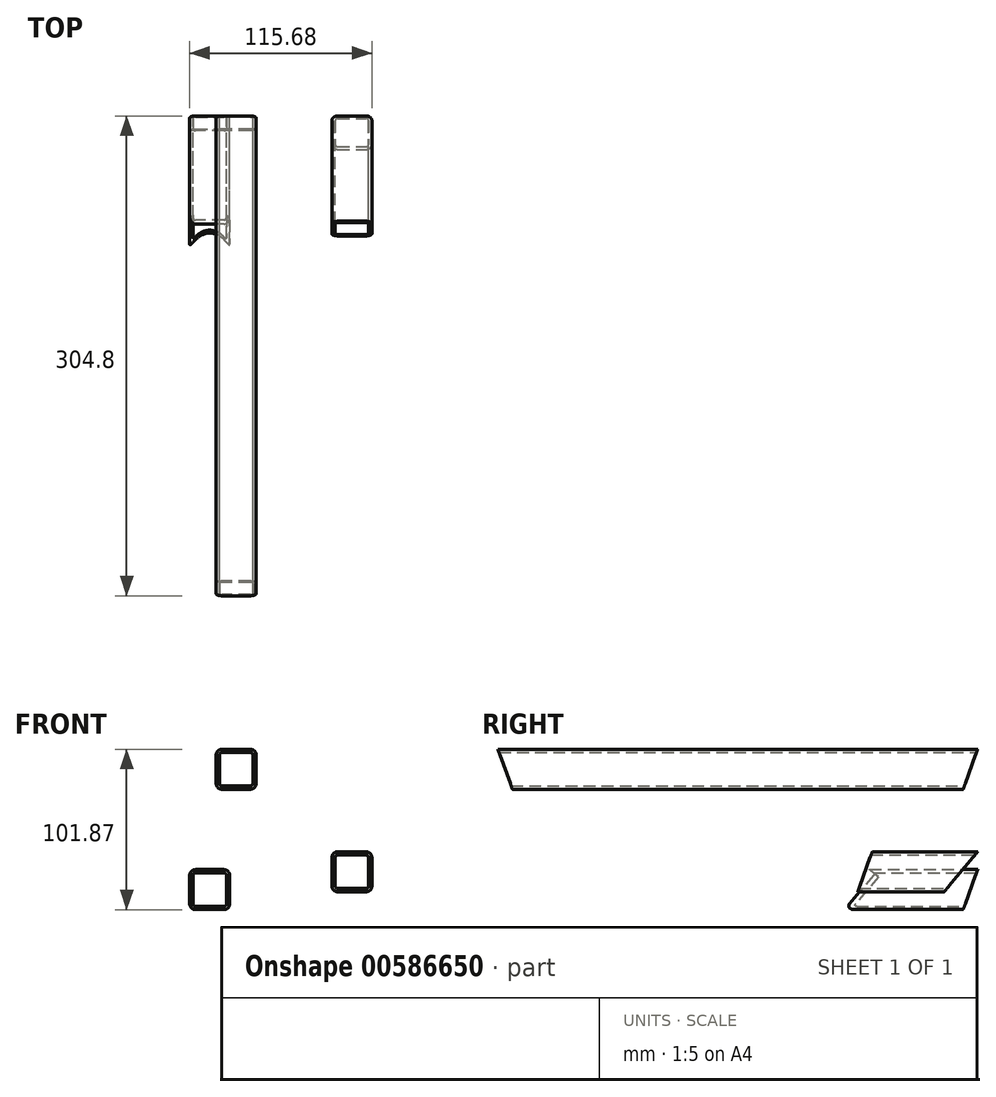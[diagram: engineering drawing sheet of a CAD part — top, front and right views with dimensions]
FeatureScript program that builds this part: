
annotation { "Feature Type Name" : "Feature", "Feature Type Description" : "" }
export const myFeature = defineFeature(function(context is Context, id is Id, definition is map)
    precondition{}
    {
        {
            var Q0;
            Q0=qCreatedBy(makeId("Front.planeOp"),FACE);
            var sketch = newSketch(context, id + "F0", { "sketchPlane" : qUnion([Q0])});
            skLineSegment(sketch, "E0.bottom", {"start": v(-55.98, 51.3) * mm, "end": v(-37.94, 51.3) * mm});
            skLineSegment(sketch, "E0.top", {"start": v(-55.98, 30.06) * mm, "end": v(-37.94, 30.06) * mm});
            skLineSegment(sketch, "E0.left", {"start": v(-57.58, 49.7) * mm, "end": v(-57.58, 31.66) * mm});
            skLineSegment(sketch, "E0.right", {"start": v(-36.34, 49.7) * mm, "end": v(-36.34, 31.66) * mm});
            skPoint(sketch, "E1.visualSharp", {"position": v(-57.58, 51.3) * mm});
            skArc(sketch, "E1.filletArc", {"start": v(-55.98, 51.3) * mm, "mid": v(-57.1, 50.83) * mm, "end": v(-57.58, 49.7) * mm});
            skPoint(sketch, "E2.visualSharp", {"position": v(-36.34, 51.3) * mm});
            skArc(sketch, "E2.filletArc", {"start": v(-36.34, 49.7) * mm, "mid": v(-36.81, 50.83) * mm, "end": v(-37.94, 51.3) * mm});
            skPoint(sketch, "E3.visualSharp", {"position": v(-36.34, 30.06) * mm});
            skArc(sketch, "E3.filletArc", {"start": v(-37.94, 30.06) * mm, "mid": v(-36.81, 30.53) * mm, "end": v(-36.34, 31.66) * mm});
            skPoint(sketch, "E4.visualSharp", {"position": v(-57.58, 30.06) * mm});
            skArc(sketch, "E4.filletArc", {"start": v(-57.58, 31.66) * mm, "mid": v(-57.1, 30.53) * mm, "end": v(-55.98, 30.06) * mm});
            skArc(sketch, "E5.0", {"start": v(-55.98, 53.38) * mm, "mid": v(-58.58, 52.3) * mm, "end": v(-59.66, 49.7) * mm});
            skLineSegment(sketch, "E5.1", {"start": v(-59.66, 49.7) * mm, "end": v(-59.66, 31.66) * mm});
            skLineSegment(sketch, "E5.2", {"start": v(-55.98, 53.38) * mm, "end": v(-37.94, 53.38) * mm});
            skArc(sketch, "E5.3", {"start": v(-59.66, 31.66) * mm, "mid": v(-58.58, 29.06) * mm, "end": v(-55.98, 27.98) * mm});
            skArc(sketch, "E5.4", {"start": v(-34.26, 49.7) * mm, "mid": v(-35.34, 52.3) * mm, "end": v(-37.94, 53.38) * mm});
            skLineSegment(sketch, "E5.5", {"start": v(-34.26, 49.7) * mm, "end": v(-34.26, 31.66) * mm});
            skArc(sketch, "E5.6", {"start": v(-37.94, 27.98) * mm, "mid": v(-35.34, 29.06) * mm, "end": v(-34.26, 31.66) * mm});
            skLineSegment(sketch, "E5.7", {"start": v(-55.98, 27.98) * mm, "end": v(-37.94, 27.98) * mm});
            skSolve(sketch);
        }
        {
            var Q0;
            Q0=makeQuery(id+"F0.imprint","IMPRINT",FACE,{"disambiguationData":[TD([[makeQuery(id+"F0.imprint","IMPRINT",EDGE,{"derivedFrom":sQuery(id+"F0.wireOp",EDGE,"E0.bottom")}),1.0]])]});
            extrude(context, id + "F1", {"entities" : qUnion([Q0]), "depth" : 304.8 * mm, "offsetDistance" : 25.4 * mm});
        }
        {
            var Q0;
            Q0=qCreatedBy(makeId("Front.planeOp"),FACE);
            var sketch = newSketch(context, id + "F2", { "sketchPlane" : qUnion([Q0])});
            skLineSegment(sketch, "E6.bottom", {"start": v(-72.76, -25.17) * mm, "end": v(-54.73, -25.17) * mm});
            skLineSegment(sketch, "E6.top", {"start": v(-72.76, -46.4) * mm, "end": v(-54.73, -46.4) * mm});
            skLineSegment(sketch, "E6.left", {"start": v(-74.36, -26.77) * mm, "end": v(-74.36, -44.8) * mm});
            skLineSegment(sketch, "E6.right", {"start": v(-53.13, -26.77) * mm, "end": v(-53.13, -44.8) * mm});
            skPoint(sketch, "E7.visualSharp", {"position": v(-74.36, -25.17) * mm});
            skArc(sketch, "E7.filletArc", {"start": v(-72.76, -25.17) * mm, "mid": v(-73.9, -25.64) * mm, "end": v(-74.36, -26.77) * mm});
            skPoint(sketch, "E8.visualSharp", {"position": v(-53.13, -25.17) * mm});
            skArc(sketch, "E8.filletArc", {"start": v(-53.13, -26.77) * mm, "mid": v(-53.6, -25.64) * mm, "end": v(-54.73, -25.17) * mm});
            skPoint(sketch, "E9.visualSharp", {"position": v(-53.13, -46.4) * mm});
            skArc(sketch, "E9.filletArc", {"start": v(-54.73, -46.4) * mm, "mid": v(-53.6, -45.94) * mm, "end": v(-53.13, -44.8) * mm});
            skPoint(sketch, "E10.visualSharp", {"position": v(-74.36, -46.4) * mm});
            skArc(sketch, "E10.filletArc", {"start": v(-74.36, -44.8) * mm, "mid": v(-73.9, -45.94) * mm, "end": v(-72.76, -46.4) * mm});
            skArc(sketch, "E11.0", {"start": v(-72.76, -23.09) * mm, "mid": v(-75.36, -24.17) * mm, "end": v(-76.44, -26.77) * mm});
            skLineSegment(sketch, "E11.1", {"start": v(-76.44, -26.77) * mm, "end": v(-76.44, -44.8) * mm});
            skLineSegment(sketch, "E11.2", {"start": v(-72.76, -23.09) * mm, "end": v(-54.73, -23.09) * mm});
            skArc(sketch, "E11.3", {"start": v(-76.44, -44.8) * mm, "mid": v(-75.36, -47.4) * mm, "end": v(-72.76, -48.49) * mm});
            skArc(sketch, "E11.4", {"start": v(-51.04, -26.77) * mm, "mid": v(-52.12, -24.17) * mm, "end": v(-54.73, -23.09) * mm});
            skLineSegment(sketch, "E11.5", {"start": v(-51.04, -26.77) * mm, "end": v(-51.04, -44.8) * mm});
            skArc(sketch, "E11.6", {"start": v(-54.73, -48.49) * mm, "mid": v(-52.12, -47.4) * mm, "end": v(-51.04, -44.8) * mm});
            skLineSegment(sketch, "E11.7", {"start": v(-72.76, -48.49) * mm, "end": v(-54.73, -48.49) * mm});
            skSolve(sketch);
        }
        {
            var Q0;
            Q0=makeQuery(id+"F2.imprint","IMPRINT",FACE,{"disambiguationData":[TD([[makeQuery(id+"F2.imprint","IMPRINT",EDGE,{"derivedFrom":sQuery(id+"F2.wireOp",EDGE,"E6.bottom")}),1.0]])]});
            extrude(context, id + "F3", {"entities" : qUnion([Q0]), "depth" : 101.6 * mm, "offsetDistance" : 25.4 * mm});
        }
        {
            var Q0;
            Q0=makeQuery(id+"F1.opExtrude","SWEPT_FACE",FACE,{"disambiguationData":[OSD([sQuery(id+"F0.wireOp",EDGE,"E5.1")])]});
            var sketch = newSketch(context, id + "F4", { "sketchPlane" : qUnion([Q0])});
            skLineSegment(sketch, "E12", {"start": v(0, 53.38) * mm, "end": v(9.24, 27.98) * mm});
            skLineSegment(sketch, "E13", {"start": v(9.24, 27.98) * mm, "end": v(0, 27.98) * mm});
            skLineSegment(sketch, "E14", {"start": v(0, 27.98) * mm, "end": v(0, 53.38) * mm});
            skLineSegment(sketch, "E15", {"start": v(152.4, 49.7) * mm, "end": v(152.4, 31.66) * mm, "construction": true});
            skLineSegment(sketch, "E16.MirrorCS", {"start": v(304.8, 53.38) * mm, "end": v(295.56, 27.98) * mm});
            skLineSegment(sketch, "E17.MirrorCS", {"start": v(304.8, 27.98) * mm, "end": v(304.8, 53.38) * mm});
            skLineSegment(sketch, "E18.MirrorCS", {"start": v(295.56, 27.98) * mm, "end": v(304.8, 27.98) * mm});
            skSolve(sketch);
        }
        {
            var Q0;
            {var subQ0=sQuery(id+"F4.wireOp",EDGE,"E12");var subQ1=sQuery(id+"F0.wireOp",EDGE,"E5.1");var subQ2=makeQuery(id+"F1.opExtrude","SWEPT_EDGE",EDGE,{"disambiguationData":[OSD([sQuery(id+"F0.wireOp",EDGE,"E5.0"),subQ1])]});var subQ3=makeQuery(id+"F4.imprint","INTERSECT",VERTEX,{"derivedFrom":[subQ2,subQ0]});Q0=makeQuery(id+"F4.imprint","IMPRINT",FACE,{"disambiguationData":[TD([[makeQuery(id+"F4.imprint","IMPRINT",EDGE,{"disambiguationData":[TD([[subQ3,-1.0]])],"derivedFrom":subQ0}),-1.0]])]});}
            var Q1;
            {var subQ0=sQuery(id+"F4.wireOp",EDGE,"E14");var subQ1=sQuery(id+"F4.wireOp",EDGE,"E12");var subQ2=makeQuery(id+"F4.imprint","INTERSECT",VERTEX,{"derivedFrom":[subQ1,subQ0]});Q1=makeQuery(id+"F4.imprint","IMPRINT",FACE,{"disambiguationData":[TD([[makeQuery(id+"F4.imprint","IMPRINT",EDGE,{"disambiguationData":[TD([[subQ2,-1.0]])],"derivedFrom":subQ1}),-1.0]])]});}
            var Q2;
            {var subQ0=sQuery(id+"F4.wireOp",EDGE,"E13");Q2=makeQuery(id+"F4.imprint","IMPRINT",FACE,{"disambiguationData":[TD([[makeQuery(id+"F4.imprint","IMPRINT",EDGE,{"derivedFrom":subQ0}),-1.0]])]});}
            var Q3;
            {var subQ0=sQuery(id+"F4.wireOp",EDGE,"E17.MirrorCS");var subQ1=sQuery(id+"F4.wireOp",EDGE,"E16.MirrorCS");var subQ2=makeQuery(id+"F4.imprint","INTERSECT",VERTEX,{"derivedFrom":[subQ1,subQ0]});Q3=makeQuery(id+"F4.imprint","IMPRINT",FACE,{"disambiguationData":[TD([[makeQuery(id+"F4.imprint","IMPRINT",EDGE,{"disambiguationData":[TD([[subQ2,-1.0]])],"derivedFrom":subQ1}),1.0]])]});}
            var Q4;
            {var subQ0=sQuery(id+"F4.wireOp",EDGE,"E16.MirrorCS");var subQ1=sQuery(id+"F0.wireOp",EDGE,"E5.1");var subQ2=makeQuery(id+"F1.opExtrude","SWEPT_EDGE",EDGE,{"disambiguationData":[OSD([sQuery(id+"F0.wireOp",EDGE,"E5.0"),subQ1])]});var subQ3=makeQuery(id+"F4.imprint","INTERSECT",VERTEX,{"derivedFrom":[subQ2,subQ0]});Q4=makeQuery(id+"F4.imprint","IMPRINT",FACE,{"disambiguationData":[TD([[makeQuery(id+"F4.imprint","IMPRINT",EDGE,{"disambiguationData":[TD([[subQ3,-1.0]])],"derivedFrom":subQ0}),1.0]])]});}
            var Q5;
            {var subQ0=sQuery(id+"F4.wireOp",EDGE,"E18.MirrorCS");Q5=makeQuery(id+"F4.imprint","IMPRINT",FACE,{"disambiguationData":[TD([[makeQuery(id+"F4.imprint","IMPRINT",EDGE,{"derivedFrom":subQ0}),1.0]])]});}
            var Q6;
            Q6=makeQuery(id+"F1.opExtrude","SWEPT_FACE",FACE,{"disambiguationData":[OSD([sQuery(id+"F0.wireOp",EDGE,"E5.5")])]});
            extrude(context, id + "F5", {"entities" : qUnion([Q0, Q1, Q2, Q3, Q4, Q5]), "operationType" : NewBodyOperationType.REMOVE, "endBound" : BoundingType.UP_TO_SURFACE, "oppositeDirection" : true, "depth" : 25.4 * mm, "endBoundEntityFace" : qUnion([Q6]), "offsetDistance" : 25.4 * mm});
        }
        {
            var Q0;
            Q0=makeQuery(id+"F3.opExtrude","SWEPT_FACE",FACE,{"disambiguationData":[OSD([sQuery(id+"F2.wireOp",EDGE,"E11.1")])]});
            var sketch = newSketch(context, id + "F6", { "sketchPlane" : qUnion([Q0])});
            skLineSegment(sketch, "E19", {"start": v(0, -23.09) * mm, "end": v(0, -48.49) * mm});
            skPoint(sketch, "E19.endSnap0", {"position": v(0, -35.79) * mm});
            skLineSegment(sketch, "E20", {"start": v(0, -48.49) * mm, "end": v(9.24, -48.49) * mm});
            skLineSegment(sketch, "E21", {"start": v(9.24, -48.49) * mm, "end": v(0, -23.09) * mm});
            skLineSegment(sketch, "E22", {"start": v(80.29, -23.09) * mm, "end": v(101.6, -48.49) * mm});
            skLineSegment(sketch, "E23", {"start": v(101.6, -48.49) * mm, "end": v(101.6, -23.09) * mm});
            skLineSegment(sketch, "E24", {"start": v(101.6, -23.09) * mm, "end": v(80.29, -23.09) * mm});
            skSolve(sketch);
        }
        {
            var Q0;
            {var subQ0=sQuery(id+"F6.wireOp",EDGE,"E19");var subQ1=sQuery(id+"F2.wireOp",EDGE,"E11.1");var subQ2=makeQuery(id+"F3.opExtrude","SWEPT_EDGE",EDGE,{"disambiguationData":[OSD([sQuery(id+"F2.wireOp",EDGE,"E11.0"),subQ1])]});var subQ3=makeQuery(id+"F6.imprint","INTERSECT",VERTEX,{"derivedFrom":[subQ2,subQ0]});Q0=makeQuery(id+"F6.imprint","IMPRINT",FACE,{"disambiguationData":[TD([[makeQuery(id+"F6.imprint","IMPRINT",EDGE,{"disambiguationData":[TD([[subQ3,-1.0]])],"derivedFrom":subQ0}),1.0]])]});}
            var Q1;
            {var subQ3=sQuery(id+"F6.wireOp",EDGE,"E20");Q1=makeQuery(id+"F6.imprint","IMPRINT",FACE,{"disambiguationData":[TD([[makeQuery(id+"F6.imprint","IMPRINT",EDGE,{"derivedFrom":subQ3}),1.0]])]});}
            var Q2;
            {var subQ0=sQuery(id+"F6.wireOp",EDGE,"E19");var subQ3=sQuery(id+"F6.wireOp",EDGE,"E21");var subQ4=makeQuery(id+"F6.imprint","INTERSECT",VERTEX,{"derivedFrom":[subQ0,subQ3]});Q2=makeQuery(id+"F6.imprint","IMPRINT",FACE,{"disambiguationData":[TD([[makeQuery(id+"F6.imprint","IMPRINT",EDGE,{"disambiguationData":[TD([[subQ4,-1.0]])],"derivedFrom":subQ0}),1.0]])]});}
            var Q3;
            {var subQ0=sQuery(id+"F6.wireOp",EDGE,"E24");Q3=makeQuery(id+"F6.imprint","IMPRINT",FACE,{"disambiguationData":[TD([[makeQuery(id+"F6.imprint","IMPRINT",EDGE,{"derivedFrom":subQ0}),1.0]])]});}
            var Q4;
            {var subQ0=sQuery(id+"F6.wireOp",EDGE,"E22");var subQ1=sQuery(id+"F2.wireOp",EDGE,"E11.1");var subQ2=makeQuery(id+"F3.opExtrude","SWEPT_EDGE",EDGE,{"disambiguationData":[OSD([sQuery(id+"F2.wireOp",EDGE,"E11.0"),subQ1])]});var subQ3=makeQuery(id+"F6.imprint","INTERSECT",VERTEX,{"derivedFrom":[subQ2,subQ0]});Q4=makeQuery(id+"F6.imprint","IMPRINT",FACE,{"disambiguationData":[TD([[makeQuery(id+"F6.imprint","IMPRINT",EDGE,{"disambiguationData":[TD([[subQ3,-1.0]])],"derivedFrom":subQ0}),1.0]])]});}
            var Q5;
            {var subQ0=sQuery(id+"F6.wireOp",EDGE,"E23");var subQ1=sQuery(id+"F6.wireOp",EDGE,"E22");var subQ2=makeQuery(id+"F6.imprint","INTERSECT",VERTEX,{"derivedFrom":[subQ1,subQ0]});Q5=makeQuery(id+"F6.imprint","IMPRINT",FACE,{"disambiguationData":[TD([[makeQuery(id+"F6.imprint","IMPRINT",EDGE,{"disambiguationData":[TD([[subQ2,1.0]])],"derivedFrom":subQ1}),1.0]])]});}
            var Q6;
            Q6=makeQuery(id+"F3.opExtrude","SWEPT_FACE",FACE,{"disambiguationData":[OSD([sQuery(id+"F2.wireOp",EDGE,"E11.5")])]});
            extrude(context, id + "F7", {"entities" : qUnion([Q0, Q1, Q2, Q3, Q4, Q5]), "operationType" : NewBodyOperationType.REMOVE, "endBound" : BoundingType.UP_TO_SURFACE, "oppositeDirection" : true, "depth" : 25.4 * mm, "endBoundEntityFace" : qUnion([Q6]), "offsetDistance" : 25.4 * mm});
        }
        {
            var Q0;
            Q0=makeQuery(id+"F7.boolean.opBoolean","COPY",FACE,{"derivedFrom":makeQuery(id+"F7.opExtrude","SWEPT_FACE",FACE,{"disambiguationData":[OSD([sQuery(id+"F6.wireOp",EDGE,"E22")])]})});
            cPlane(context, id + "F8", {"entities" : qUnion([Q0]), "cplaneType" : CPlaneType.OFFSET, "offset" : 25.4 * mm, "width" : 152.4 * mm, "height" : 152.4 * mm});
        }
        {
            var Q0;
            Q0=makeQuery(id+"F7.boolean.opBoolean","MERGE",EDGE,{"derivedFrom":[makeQuery(id+"F3.opExtrude","CAP_EDGE",EDGE,{"disambiguationData":[OSD([sQuery(id+"F2.wireOp",EDGE,"E11.7")])],"isStart":false}),makeQuery(id+"F7.opExtrude","SWEPT_EDGE",EDGE,{"disambiguationData":[OSD([sQuery(id+"F6.wireOp",EDGE,"E22"),sQuery(id+"F6.wireOp",EDGE,"E23")])]})]});
            var Q1;
            Q1=qCreatedBy(id+"F8.planeOp",FACE);
            cPlane(context, id + "F9", {"entities" : qUnion([Q0, Q1]), "cplaneType" : CPlaneType.LINE_ANGLE, "offset" : 25.4 * mm, "angle" : 90 * degree, "width" : 152.4 * mm, "height" : 152.4 * mm});
        }
        {
            var Q0;
            Q0=qCreatedBy(id+"F9.planeOp",FACE);
            var sketch = newSketch(context, id + "F10", { "sketchPlane" : qUnion([Q0])});
            skCircle(sketch, "E25", {"center": v(-63.74, -40.12) * mm, "radius": 14.29 * mm});
            skSolve(sketch);
        }
        {
            var Q0;
            Q0=makeQuery(id+"F10.imprint","IMPRINT",FACE,{"disambiguationData":[TD([[makeQuery(id+"F10.imprint","IMPRINT",EDGE,{"derivedFrom":sQuery(id+"F10.wireOp",EDGE,"E25")}),1.0]])]});
            extrude(context, id + "F11", {"entities" : qUnion([Q0]), "operationType" : NewBodyOperationType.REMOVE, "depth" : 40.64 * mm, "offsetDistance" : 25.4 * mm});
        }
        {
            var Q0;
            Q0=qCreatedBy(makeId("Front.planeOp"),FACE);
            var sketch = newSketch(context, id + "F12", { "sketchPlane" : qUnion([Q0])});
            skLineSegment(sketch, "E26.bottom", {"start": v(17.53, -13.84) * mm, "end": v(35.56, -13.84) * mm});
            skLineSegment(sketch, "E26.top", {"start": v(17.53, -35.08) * mm, "end": v(35.56, -35.08) * mm});
            skLineSegment(sketch, "E26.left", {"start": v(15.93, -15.44) * mm, "end": v(15.93, -33.48) * mm});
            skLineSegment(sketch, "E26.right", {"start": v(37.16, -15.44) * mm, "end": v(37.16, -33.48) * mm});
            skPoint(sketch, "E27.visualSharp", {"position": v(15.93, -13.84) * mm});
            skArc(sketch, "E27.filletArc", {"start": v(17.53, -13.84) * mm, "mid": v(16.4, -14.31) * mm, "end": v(15.93, -15.44) * mm});
            skPoint(sketch, "E28.visualSharp", {"position": v(37.16, -13.84) * mm});
            skArc(sketch, "E28.filletArc", {"start": v(37.16, -15.44) * mm, "mid": v(36.7, -14.31) * mm, "end": v(35.56, -13.84) * mm});
            skPoint(sketch, "E29.visualSharp", {"position": v(37.16, -35.08) * mm});
            skArc(sketch, "E29.filletArc", {"start": v(35.56, -35.08) * mm, "mid": v(36.7, -34.6) * mm, "end": v(37.16, -33.48) * mm});
            skPoint(sketch, "E30.visualSharp", {"position": v(15.93, -35.08) * mm});
            skArc(sketch, "E30.filletArc", {"start": v(15.93, -33.48) * mm, "mid": v(16.4, -34.6) * mm, "end": v(17.53, -35.08) * mm});
            skArc(sketch, "E31.0", {"start": v(17.53, -11.76) * mm, "mid": v(14.92, -12.84) * mm, "end": v(13.84, -15.44) * mm});
            skLineSegment(sketch, "E31.1", {"start": v(13.84, -15.44) * mm, "end": v(13.84, -33.48) * mm});
            skLineSegment(sketch, "E31.2", {"start": v(17.53, -11.76) * mm, "end": v(35.56, -11.76) * mm});
            skArc(sketch, "E31.3", {"start": v(13.84, -33.48) * mm, "mid": v(14.92, -36.08) * mm, "end": v(17.53, -37.16) * mm});
            skArc(sketch, "E31.4", {"start": v(39.24, -15.44) * mm, "mid": v(38.17, -12.84) * mm, "end": v(35.56, -11.76) * mm});
            skLineSegment(sketch, "E31.5", {"start": v(39.24, -15.44) * mm, "end": v(39.24, -33.48) * mm});
            skArc(sketch, "E31.6", {"start": v(35.56, -37.16) * mm, "mid": v(38.17, -36.08) * mm, "end": v(39.24, -33.48) * mm});
            skLineSegment(sketch, "E31.7", {"start": v(17.53, -37.16) * mm, "end": v(35.56, -37.16) * mm});
            skSolve(sketch);
        }
        {
            var Q0;
            Q0=makeQuery(id+"F12.imprint","IMPRINT",FACE,{"disambiguationData":[TD([[makeQuery(id+"F12.imprint","IMPRINT",EDGE,{"derivedFrom":sQuery(id+"F12.wireOp",EDGE,"E26.bottom")}),1.0]])]});
            extrude(context, id + "F13", {"entities" : qUnion([Q0]), "depth" : 76.2 * mm, "offsetDistance" : 25.4 * mm});
        }
        {
            var Q0;
            Q0=makeQuery(id+"F13.opExtrude","SWEPT_FACE",FACE,{"disambiguationData":[OSD([sQuery(id+"F12.wireOp",EDGE,"E31.5")])]});
            var sketch = newSketch(context, id + "F14", { "sketchPlane" : qUnion([Q0])});
            skLineSegment(sketch, "E32", {"start": v(0, -11.76) * mm, "end": v(-21.31, -37.16) * mm});
            skLineSegment(sketch, "E33", {"start": v(-21.31, -37.16) * mm, "end": v(0, -37.16) * mm});
            skLineSegment(sketch, "E34", {"start": v(0, -37.16) * mm, "end": v(0, -11.76) * mm});
            skLineSegment(sketch, "E35", {"start": v(-76.2, -11.76) * mm, "end": v(-76.2, -37.16) * mm});
            skLineSegment(sketch, "E36", {"start": v(-76.2, -37.16) * mm, "end": v(-66.96, -11.76) * mm});
            skLineSegment(sketch, "E37", {"start": v(-66.96, -11.76) * mm, "end": v(-76.2, -11.76) * mm});
            skSolve(sketch);
        }
        {
            var Q0;
            {var subQ3=sQuery(id+"F14.wireOp",EDGE,"E37");Q0=makeQuery(id+"F14.imprint","IMPRINT",FACE,{"disambiguationData":[TD([[makeQuery(id+"F14.imprint","IMPRINT",EDGE,{"derivedFrom":subQ3}),1.0]])]});}
            var Q1;
            {var subQ0=sQuery(id+"F14.wireOp",EDGE,"E35");var subQ1=sQuery(id+"F12.wireOp",EDGE,"E31.5");var subQ2=makeQuery(id+"F13.opExtrude","SWEPT_EDGE",EDGE,{"disambiguationData":[OSD([sQuery(id+"F12.wireOp",EDGE,"E31.4"),subQ1])]});var subQ3=makeQuery(id+"F14.imprint","INTERSECT",VERTEX,{"derivedFrom":[subQ2,subQ0]});Q1=makeQuery(id+"F14.imprint","IMPRINT",FACE,{"disambiguationData":[TD([[makeQuery(id+"F14.imprint","IMPRINT",EDGE,{"disambiguationData":[TD([[subQ3,-1.0]])],"derivedFrom":subQ0}),1.0]])]});}
            var Q2;
            {var subQ0=sQuery(id+"F14.wireOp",EDGE,"E35");var subQ3=sQuery(id+"F14.wireOp",EDGE,"E36");var subQ4=makeQuery(id+"F14.imprint","INTERSECT",VERTEX,{"derivedFrom":[subQ0,subQ3]});Q2=makeQuery(id+"F14.imprint","IMPRINT",FACE,{"disambiguationData":[TD([[makeQuery(id+"F14.imprint","IMPRINT",EDGE,{"disambiguationData":[TD([[subQ4,1.0]])],"derivedFrom":subQ0}),1.0]])]});}
            var Q3;
            {var subQ0=sQuery(id+"F14.wireOp",EDGE,"E33");Q3=makeQuery(id+"F14.imprint","IMPRINT",FACE,{"disambiguationData":[TD([[makeQuery(id+"F14.imprint","IMPRINT",EDGE,{"derivedFrom":subQ0}),1.0]])]});}
            var Q4;
            {var subQ0=sQuery(id+"F14.wireOp",EDGE,"E32");var subQ1=sQuery(id+"F12.wireOp",EDGE,"E31.5");var subQ2=makeQuery(id+"F13.opExtrude","SWEPT_EDGE",EDGE,{"disambiguationData":[OSD([sQuery(id+"F12.wireOp",EDGE,"E31.4"),subQ1])]});var subQ3=makeQuery(id+"F14.imprint","INTERSECT",VERTEX,{"derivedFrom":[subQ2,subQ0]});Q4=makeQuery(id+"F14.imprint","IMPRINT",FACE,{"disambiguationData":[TD([[makeQuery(id+"F14.imprint","IMPRINT",EDGE,{"disambiguationData":[TD([[subQ3,-1.0]])],"derivedFrom":subQ0}),1.0]])]});}
            var Q5;
            {var subQ0=sQuery(id+"F14.wireOp",EDGE,"E34");var subQ1=sQuery(id+"F14.wireOp",EDGE,"E32");var subQ2=makeQuery(id+"F14.imprint","INTERSECT",VERTEX,{"derivedFrom":[subQ1,subQ0]});Q5=makeQuery(id+"F14.imprint","IMPRINT",FACE,{"disambiguationData":[TD([[makeQuery(id+"F14.imprint","IMPRINT",EDGE,{"disambiguationData":[TD([[subQ2,-1.0]])],"derivedFrom":subQ1}),1.0]])]});}
            var Q6;
            Q6=makeQuery(id+"F13.opExtrude","SWEPT_FACE",FACE,{"disambiguationData":[OSD([sQuery(id+"F12.wireOp",EDGE,"E31.1")])]});
            extrude(context, id + "F15", {"entities" : qUnion([Q0, Q1, Q2, Q3, Q4, Q5]), "operationType" : NewBodyOperationType.REMOVE, "endBound" : BoundingType.UP_TO_SURFACE, "oppositeDirection" : true, "depth" : 25.4 * mm, "endBoundEntityFace" : qUnion([Q6]), "offsetDistance" : 25.4 * mm});
        }
    });
